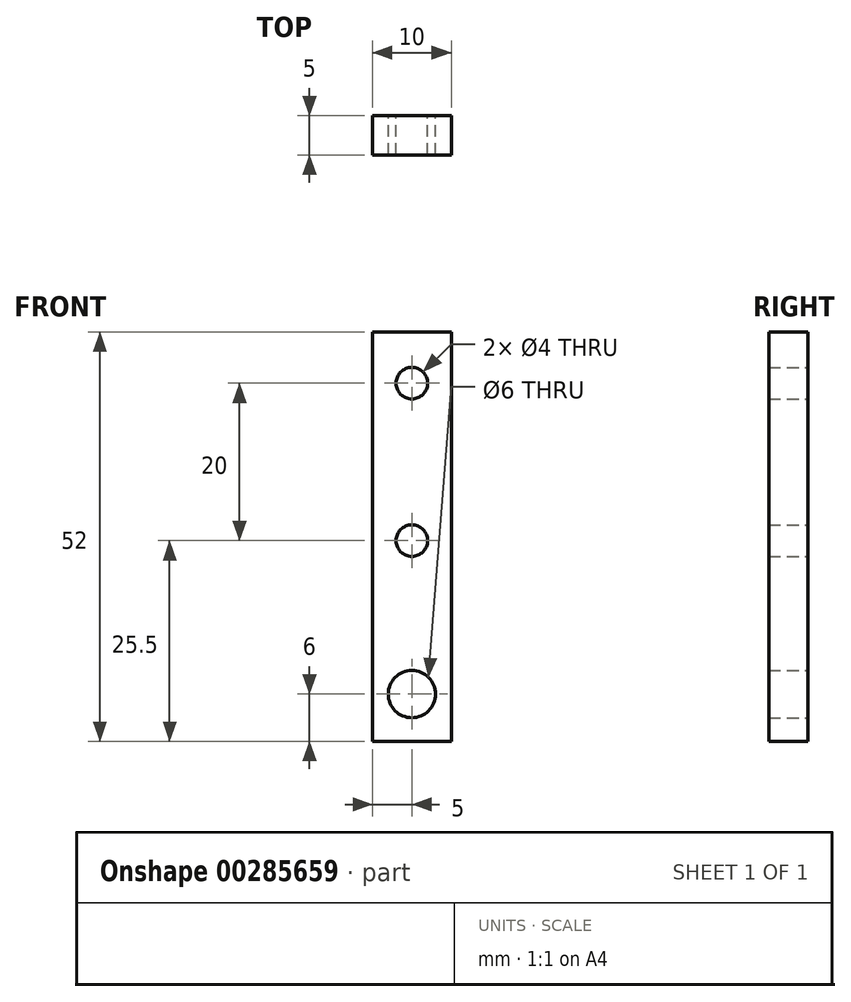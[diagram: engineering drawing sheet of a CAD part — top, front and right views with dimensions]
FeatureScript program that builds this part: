
annotation { "Feature Type Name" : "Feature", "Feature Type Description" : "" }
export const myFeature = defineFeature(function(context is Context, id is Id, definition is map)
    precondition{}
    {
        {
            var Q0;
            Q0=qCreatedBy(makeId("Front.planeOp"),FACE);
            var sketch = newSketch(context, id + "F0", { "sketchPlane" : qUnion([Q0])});
            skLineSegment(sketch, "E0.bottom", {"start": v(5, -6) * mm, "end": v(-5, -6) * mm});
            skLineSegment(sketch, "E0.left", {"start": v(5, -6) * mm, "end": v(5, 6) * mm});
            skLineSegment(sketch, "E0.right", {"start": v(-5, -6) * mm, "end": v(-5, 6) * mm});
            skPoint(sketch, "E0.middle", {"position": v(0, 0) * mm});
            skCircle(sketch, "E1", {"center": v(0, 0) * mm, "radius": 3 * mm});
            skLineSegment(sketch, "E2.top", {"start": v(-5, 46) * mm, "end": v(5, 46) * mm});
            skLineSegment(sketch, "E2.left", {"start": v(-5, 6) * mm, "end": v(-5, 46) * mm});
            skLineSegment(sketch, "E2.right", {"start": v(5, 6) * mm, "end": v(5, 46) * mm});
            skCircle(sketch, "E3", {"center": v(0, 39.5) * mm, "radius": 2 * mm});
            skCircle(sketch, "E4", {"center": v(0, 19.5) * mm, "radius": 2 * mm});
            skSolve(sketch);
        }
        {
            var Q0;
            Q0=makeQuery(id+"F0.imprint","IMPRINT",FACE,{"disambiguationData":[TD([[makeQuery(id+"F0.imprint","IMPRINT",EDGE,{"derivedFrom":sQuery(id+"F0.wireOp",EDGE,"E0.bottom")}),-1.0]])]});
            extrude(context, id + "F1", {"entities" : qUnion([Q0]), "depth" : 5 * mm, "offsetDistance" : 25 * mm});
        }
    });
